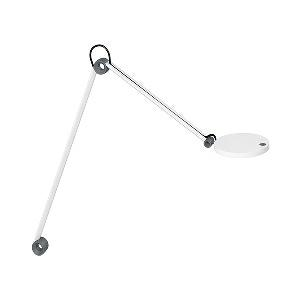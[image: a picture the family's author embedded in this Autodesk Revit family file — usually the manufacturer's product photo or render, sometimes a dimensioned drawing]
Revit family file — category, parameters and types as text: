
# Revit family: para_mi_-_ftl_102_r__930_00628572_5ce1
name_source: partatom
category: Lighting Fixtures
units: mm (PartAtom-declared; Revit-internal decimal feet)

## family parameters
Cut with Voids When Loaded = No
Host = Face
Light Source = No
Part Type = Normal
Room Calculation Point = No
Round Connector Dimension = Use Diameter
Shared = No

## types (1)
- PARA.MI - FTL 102 R /930 (1 x LED, 580 lm, 3000K)
    Apparent Load = 7 VA
    Approval mark = CE
    CIE Flux Codes = 69 94 99 100 100
    Color Rendering = 90-100
    Color Temperature = 3000K
    Control Gear = Electronic ballast
    Default Elevation = 1800 mm
    Description = FTL 102 R|Task luminaire|light source: LED|work equipment: Electronic plug-in transformer|connected load: 100-240 V, 50/60 Hz|Power consumption: approx. 7 W|luminous flux: 580 lm|luminous efficacy: 82 lm/W|Illuminance efficiency factor: 107 lx/W|colour temperature: Warm white, ca. 3000 K|color rendering index (CRI): >= 90|chromaticity tolerance:  3 SDCM|class of protection: II with plug-in power supply, III without plug-in power supply|technology: Continuously dimmable|luminaire body|material: Aluminium|surface: Painted|colour: White|lamp cover: Plastic, Clear|tubular sections|material: Tubular aluminium section|surface: Painted|colour: White|weight (net): approx. 1.0 kg|mains lead: 3.00 m Mains plug BS 1363, CEE 7/XVI, NEMA 1-15P|Fastening: Adaptor (accessory), Table base (accessory), Table clamp (accessory), Tap16|glare control: Reflector|special features: Automatic switchoff adjustable, Push button in luminaire head, Behaviour at net recovery adjustable|Approval mark: C - ETL - US (F. CAN U. USA), VDE - ENEC SEP LIGHT & POWER SUPPLY UNIT|
    Height = 12 mm  [stored 0.0393701 ft]
    Lamp = 1 x LED
    Lamp Light Flux = 580 lm
    Lamp count = 1
    Length = 123 mm
    Luminous efficacy = 83 lm/W
    Manufacturer = Waldmann
    ModVariant = No
    Model = 00628572
    Mounting Place = Table
    Mounting Type = Surface mounted
    Number of Poles = 1
    OnlyDefault = Yes
    Power Factor = 1
    Product Name = PARA.MI - FTL 102 R /930
    Product group = Task luminaire (office)
    ProductGroupID = 21
    Protection Class = Protection class II
    Protection Degree = IP 40
    RLX_Detail_Level = 1
    RLX_Emergency_Light_Flux = 0 lm
    RLX_Emergency_Type = 0
    RLX_Emergency_Type_DB = No
    RlxData = <blob elided: 73429 chars, md5=38c80edc>
    Socket = socket
    Standby Power = 0 W
    System Light Flux = 580 lm
    System Power = 7 W
    Type Comments = Product without accessories
    Type Image = 113147000-00638507.jpg
    URL = http://relux.com
    VarID = ---
    Voltage = 230 V
    Voltage Range = 220-240 V
    Weight = 0.00 kg
    Width = 0 mm  [stored 0 ft]

note: [stored X ft] marks values corroborated as IEEE doubles in the binary element streams (Revit-internal decimal feet)

## geometry (parser evidence)
native form markers: Blend x4, Sweep x16
no freeform markers — native parametric forms only
